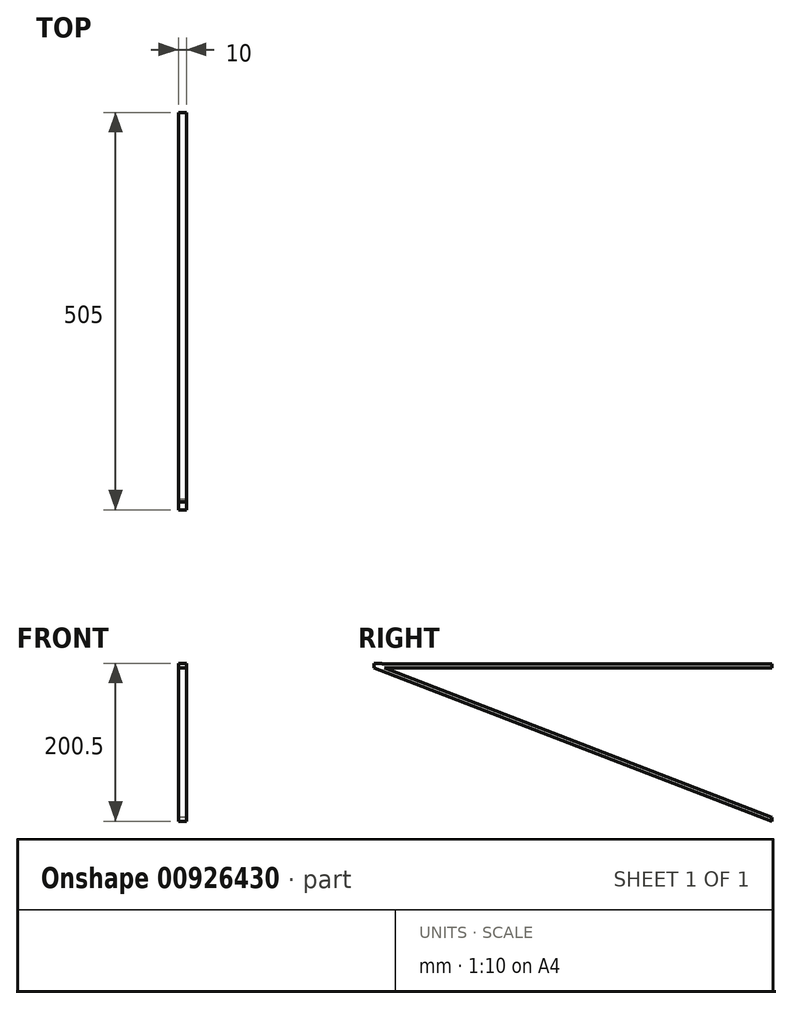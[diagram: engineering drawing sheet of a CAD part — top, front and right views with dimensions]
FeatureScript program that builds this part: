
annotation { "Feature Type Name" : "Feature", "Feature Type Description" : "" }
export const myFeature = defineFeature(function(context is Context, id is Id, definition is map)
    precondition{}
    {
        {
            var Q0;
            Q0=qCreatedBy(makeId("Front.planeOp"),FACE);
            var sketch = newSketch(context, id + "F0", { "sketchPlane" : qUnion([Q0])});
            skLineSegment(sketch, "E0", {"start": v(0, 0) * mm, "end": v(-5, 0) * mm});
            skLineSegment(sketch, "E1.MirrorCS", {"start": v(0, 0) * mm, "end": v(5, 0) * mm});
            skLineSegment(sketch, "E2", {"start": v(5, 0) * mm, "end": v(5, -200) * mm});
            skLineSegment(sketch, "E3.MirrorCS", {"start": v(-5, 0) * mm, "end": v(-5, -200) * mm});
            skLineSegment(sketch, "E4", {"start": v(5, -200) * mm, "end": v(-5, -200) * mm});
            skPoint(sketch, "E5", {"position": v(5, 0) * mm});
            skPoint(sketch, "E6", {"position": v(-5, 0) * mm});
            skSolve(sketch);
        }
        {
            var Q0;
            Q0=makeQuery(id+"F0.imprint","IMPRINT",FACE,{"disambiguationData":[TD([[makeQuery(id+"F0.imprint","IMPRINT",EDGE,{"derivedFrom":sQuery(id+"F0.wireOp",EDGE,"E0")}),1.0]])]});
            extrude(context, id + "F1", {"entities" : qUnion([Q0]), "depth" : 505 * mm, "offsetDistance" : 25 * mm});
        }
        {
            var Q0;
            Q0=qSketchRegion(id+"F0",true);
            extrude(context, id + "F2", {"entities" : qUnion([Q0]), "operationType" : NewBodyOperationType.ADD, "depth" : 500.5 * mm, "offsetDistance" : 25 * mm});
        }
        {
            var Q0;
            Q0=makeQuery(id+"F1.opExtrude","SWEPT_FACE",FACE,{"disambiguationData":[OSD([sQuery(id+"F0.wireOp",EDGE,"E3.MirrorCS")])]});
            var sketch = newSketch(context, id + "F3", { "sketchPlane" : qUnion([Q0])});
            skLineSegment(sketch, "E7", {"start": v(505, 0) * mm, "end": v(505, -5) * mm});
            skLineSegment(sketch, "E8", {"start": v(0, 0) * mm, "end": v(0, -5) * mm});
            skLineSegment(sketch, "E9", {"start": v(0, -5) * mm, "end": v(505, -5) * mm});
            skLineSegment(sketch, "E10", {"start": v(0, -200) * mm, "end": v(0, -195) * mm});
            skLineSegment(sketch, "E11", {"start": v(0, -195) * mm, "end": v(505, 0) * mm});
            skLineSegment(sketch, "E12", {"start": v(0, -200) * mm, "end": v(505, -5) * mm});
            skPoint(sketch, "E13", {"position": v(492.05, -5) * mm});
            skLineSegment(sketch, "E14", {"start": v(492.05, -5) * mm, "end": v(331.35, -5) * mm});
            skLineSegment(sketch, "E15", {"start": v(331.35, -5) * mm, "end": v(333.85, -5) * mm});
            skLineSegment(sketch, "E16", {"start": v(331.35, -5) * mm, "end": v(328.85, -5) * mm});
            skLineSegment(sketch, "E17", {"start": v(328.85, -5) * mm, "end": v(328.85, -65.32) * mm});
            skLineSegment(sketch, "E18", {"start": v(333.85, -5) * mm, "end": v(333.85, -66.09) * mm});
            skLineSegment(sketch, "E19", {"start": v(331.35, -5) * mm, "end": v(170.65, -5) * mm});
            skLineSegment(sketch, "E20", {"start": v(170.65, -5) * mm, "end": v(173.15, -5) * mm});
            skLineSegment(sketch, "E21", {"start": v(170.65, -5) * mm, "end": v(168.15, -5) * mm});
            skLineSegment(sketch, "E22", {"start": v(168.15, -5) * mm, "end": v(168.15, -130.07) * mm});
            skLineSegment(sketch, "E23", {"start": v(173.15, -7.7) * mm, "end": v(173.15, -128.14) * mm});
            skLineSegment(sketch, "E24", {"start": v(331.35, -67.05) * mm, "end": v(331.35, -83.15) * mm});
            skLineSegment(sketch, "E25", {"start": v(179.81, -5) * mm, "end": v(328.85, -65.32) * mm});
            skLineSegment(sketch, "E26", {"start": v(172.21, -7.32) * mm, "end": v(325.44, -69.33) * mm});
            skSolve(sketch);
        }
        {
            var Q0;
            {var subQ0=sQuery(id+"F3.wireOp",EDGE,"E17");Q0=makeQuery(id+"F3.imprint","IMPRINT",FACE,{"disambiguationData":[TD([[makeQuery(id+"F3.imprint","IMPRINT",EDGE,{"derivedFrom":subQ0}),-1.0]])]});}
            var Q1;
            {var subQ0=sQuery(id+"F3.wireOp",EDGE,"E23");Q1=makeQuery(id+"F3.imprint","IMPRINT",FACE,{"disambiguationData":[TD([[makeQuery(id+"F3.imprint","IMPRINT",EDGE,{"derivedFrom":subQ0}),1.0]])]});}
            var Q2;
            {var subQ3=sQuery(id+"F3.wireOp",EDGE,"E22");Q2=makeQuery(id+"F3.imprint","IMPRINT",FACE,{"disambiguationData":[TD([[makeQuery(id+"F3.imprint","IMPRINT",EDGE,{"derivedFrom":subQ3}),-1.0]])]});}
            var Q3;
            {var subQ0=sQuery(id+"F3.wireOp",EDGE,"E18");Q3=makeQuery(id+"F3.imprint","IMPRINT",FACE,{"disambiguationData":[TD([[makeQuery(id+"F3.imprint","IMPRINT",EDGE,{"derivedFrom":subQ0}),1.0]])]});}
            extrude(context, id + "F4", {"entities" : qUnion([Q0, Q1, Q2, Q3]), "operationType" : NewBodyOperationType.REMOVE, "endBound" : BoundingType.UP_TO_NEXT, "oppositeDirection" : true, "depth" : 25 * mm, "offsetDistance" : 25 * mm});
        }
        {
            var Q0;
            {var subQ1=sQuery(id+"F0.wireOp",EDGE,"E3.MirrorCS");var subQ2=makeQuery(id+"F1.opExtrude","SWEPT_EDGE",EDGE,{"disambiguationData":[OSD([subQ1,sQuery(id+"F0.wireOp",EDGE,"E4")])]});Q0=makeQuery(id+"F3.imprint","IMPRINT",FACE,{"disambiguationData":[TD([[makeQuery(id+"F3.imprint","IMPRINT",EDGE,{"derivedFrom":subQ2}),-1.0]])]});}
            extrude(context, id + "F5", {"entities" : qUnion([Q0]), "operationType" : NewBodyOperationType.REMOVE, "endBound" : BoundingType.UP_TO_NEXT, "oppositeDirection" : true, "depth" : 25 * mm, "offsetDistance" : 25 * mm});
        }
        {
            var Q0;
            Q0=makeQuery(id+"F1.opExtrude","SWEPT_FACE",FACE,{"disambiguationData":[OSD([sQuery(id+"F0.wireOp",EDGE,"E3.MirrorCS")])]});
            var sketch = newSketch(context, id + "F6", { "sketchPlane" : qUnion([Q0])});
            skLineSegment(sketch, "E27", {"start": v(168.15, -5) * mm, "end": v(179.81, -5) * mm});
            skLineSegment(sketch, "E28", {"start": v(328.85, -5) * mm, "end": v(333.85, -5) * mm});
            skLineSegment(sketch, "E29", {"start": v(325.44, -69.33) * mm, "end": v(333.85, -66.09) * mm});
            skLineSegment(sketch, "E30", {"start": v(168.15, -130.07) * mm, "end": v(173.15, -128.14) * mm});
            skSolve(sketch);
        }
        {
            var Q0;
            Q0=makeQuery(id+"F6.imprint","IMPRINT",FACE,{"disambiguationData":[TD([[makeQuery(id+"F6.imprint","IMPRINT",EDGE,{"derivedFrom":sQuery(id+"F6.wireOp",EDGE,"E27")}),-1.0]])]});
            extrude(context, id + "F7", {"entities" : qUnion([Q0]), "operationType" : NewBodyOperationType.REMOVE, "oppositeDirection" : true, "depth" : 3.5 * mm, "offsetDistance" : 25 * mm});
        }
        {
            var Q0;
            Q0=makeQuery(id+"F1.opExtrude","SWEPT_FACE",FACE,{"disambiguationData":[OSD([sQuery(id+"F0.wireOp",EDGE,"E0"),sQuery(id+"F0.wireOp",EDGE,"E1.MirrorCS")])]});
            var sketch = newSketch(context, id + "F8", { "sketchPlane" : qUnion([Q0])});
            skLineSegment(sketch, "E31.bottom", {"start": v(-5, -505) * mm, "end": v(5, -505) * mm});
            skLineSegment(sketch, "E31.top", {"start": v(-5, -495) * mm, "end": v(5, -495) * mm});
            skLineSegment(sketch, "E31.left", {"start": v(-5, -505) * mm, "end": v(-5, -495) * mm});
            skLineSegment(sketch, "E31.right", {"start": v(5, -505) * mm, "end": v(5, -495) * mm});
            skSolve(sketch);
        }
        {
            var Q0;
            Q0=makeQuery(id+"F1.opExtrude","SWEPT_FACE",FACE,{"disambiguationData":[OSD([sQuery(id+"F0.wireOp",EDGE,"E2")])]});
            var sketch = newSketch(context, id + "F9", { "sketchPlane" : qUnion([Q0])});
            skLineSegment(sketch, "E32", {"start": v(-173.15, -128.14) * mm, "end": v(-168.15, -130.07) * mm});
            skLineSegment(sketch, "E33", {"start": v(-325.44, -69.33) * mm, "end": v(-333.85, -66.09) * mm});
            skLineSegment(sketch, "E34", {"start": v(-333.85, -5) * mm, "end": v(-328.85, -5) * mm});
            skLineSegment(sketch, "E35", {"start": v(-168.15, -5) * mm, "end": v(-179.81, -5) * mm});
            skSolve(sketch);
        }
        {
            var Q0;
            Q0=makeQuery(id+"F8.imprint","IMPRINT",FACE,{"disambiguationData":[TD([[makeQuery(id+"F8.imprint","IMPRINT",EDGE,{"derivedFrom":sQuery(id+"F8.wireOp",EDGE,"E31.bottom")}),1.0]])]});
            extrude(context, id + "F10", {"entities" : qUnion([Q0]), "operationType" : NewBodyOperationType.ADD, "depth" : 0.5 * mm, "offsetDistance" : 25 * mm});
        }
        {
            var Q0;
            Q0=makeQuery(id+"F9.imprint","IMPRINT",FACE,{"disambiguationData":[TD([[makeQuery(id+"F9.imprint","IMPRINT",EDGE,{"derivedFrom":sQuery(id+"F9.wireOp",EDGE,"E32")}),1.0]])]});
            extrude(context, id + "F11", {"entities" : qUnion([Q0]), "operationType" : NewBodyOperationType.REMOVE, "oppositeDirection" : true, "depth" : 3.5 * mm, "offsetDistance" : 25 * mm});
        }
        {
            var Q0;
            {var subQ0=sQuery(id+"F3.wireOp",EDGE,"E9");Q0=makeQuery(id+"F11.boolean.opBoolean","MERGE",FACE,{"derivedFrom":[makeQuery(id+"F7.boolean.opBoolean","MERGE",FACE,{"derivedFrom":[makeQuery(id+"F4.boolean.opBoolean","COPY",FACE,{"derivedFrom":makeQuery(id+"F4.opExtrude","SWEPT_FACE",FACE,{"disambiguationData":[OSD([subQ0]),TDD([makeQuery(id+"F3.imprint","IMPRINT",EDGE,{"disambiguationData":[TD([[makeQuery(id+"F3.imprint","INTERSECT",VERTEX,{"derivedFrom":[subQ0,sQuery(id+"F3.wireOp",EDGE,"E22")]}),1.0]])],"derivedFrom":subQ0})])]})}),makeQuery(id+"F4.boolean.opBoolean","COPY",FACE,{"derivedFrom":makeQuery(id+"F4.opExtrude","SWEPT_FACE",FACE,{"disambiguationData":[OSD([subQ0]),TDD([makeQuery(id+"F3.imprint","IMPRINT",EDGE,{"disambiguationData":[TD([[makeQuery(id+"F3.imprint","INTERSECT",VERTEX,{"derivedFrom":[subQ0,sQuery(id+"F3.wireOp",EDGE,"E18")]}),-1.0]])],"derivedFrom":subQ0})])]})}),makeQuery(id+"F4.boolean.opBoolean","COPY",FACE,{"derivedFrom":makeQuery(id+"F4.opExtrude","SWEPT_FACE",FACE,{"disambiguationData":[OSD([subQ0]),TDD([makeQuery(id+"F3.imprint","IMPRINT",EDGE,{"disambiguationData":[TD([[makeQuery(id+"F3.imprint","INTERSECT",VERTEX,{"derivedFrom":[subQ0,sQuery(id+"F3.wireOp",EDGE,"E17")]}),1.0]])],"derivedFrom":subQ0})])]})})],"fromTools":[makeQuery(id+"F7.opExtrude","SWEPT_FACE",FACE,{"disambiguationData":[OSD([sQuery(id+"F6.wireOp",EDGE,"E27")])]}),makeQuery(id+"F7.opExtrude","SWEPT_FACE",FACE,{"disambiguationData":[OSD([sQuery(id+"F6.wireOp",EDGE,"E28")])]})]})],"fromTools":[makeQuery(id+"F11.opExtrude","SWEPT_FACE",FACE,{"disambiguationData":[OSD([sQuery(id+"F9.wireOp",EDGE,"E34")])]}),makeQuery(id+"F11.opExtrude","SWEPT_FACE",FACE,{"disambiguationData":[OSD([sQuery(id+"F9.wireOp",EDGE,"E35")])]})]});}
            var sketch = newSketch(context, id + "F12", { "sketchPlane" : qUnion([Q0])});
            skLineSegment(sketch, "E36", {"start": v(1.5, 0) * mm, "end": v(1.5, 492.05) * mm});
            skLineSegment(sketch, "E37", {"start": v(-1.5, 0) * mm, "end": v(1.5, 0) * mm});
            skLineSegment(sketch, "E38", {"start": v(-1.5, 0) * mm, "end": v(-1.5, 492.05) * mm});
            skLineSegment(sketch, "E39", {"start": v(1.5, 492.05) * mm, "end": v(-1.5, 492.05) * mm});
            skSolve(sketch);
        }
        {
            var Q0;
            {var subQ3=sQuery(id+"F12.wireOp",EDGE,"E39");Q0=makeQuery(id+"F12.imprint","IMPRINT",FACE,{"disambiguationData":[TD([[makeQuery(id+"F12.imprint","IMPRINT",EDGE,{"derivedFrom":subQ3}),1.0]])]});}
            var Q1;
            {var subQ1=sQuery(id+"F3.wireOp",EDGE,"E9");var subQ2=makeQuery(id+"F4.boolean.opBoolean","COPY",EDGE,{"derivedFrom":makeQuery(id+"F4.opExtrude","SWEPT_EDGE",EDGE,{"disambiguationData":[OSD([subQ1,sQuery(id+"F3.wireOp",EDGE,"E17")])]})});Q1=makeQuery(id+"F12.imprint","IMPRINT",FACE,{"disambiguationData":[TD([[makeQuery(id+"F12.imprint","IMPRINT",EDGE,{"derivedFrom":subQ2}),1.0]])]});}
            var Q2;
            {var subQ3=sQuery(id+"F12.wireOp",EDGE,"E37");Q2=makeQuery(id+"F12.imprint","IMPRINT",FACE,{"disambiguationData":[TD([[makeQuery(id+"F12.imprint","IMPRINT",EDGE,{"derivedFrom":subQ3}),-1.0]])]});}
            extrude(context, id + "F13", {"entities" : qUnion([Q0, Q1, Q2]), "operationType" : NewBodyOperationType.ADD, "depth" : 3 * mm, "offsetDistance" : 25 * mm});
        }
        {
            var Q0;
            {var subQ0=sQuery(id+"F3.wireOp",EDGE,"E11");Q0=makeQuery(id+"F11.boolean.opBoolean","MERGE",FACE,{"derivedFrom":[makeQuery(id+"F7.boolean.opBoolean","MERGE",FACE,{"derivedFrom":[makeQuery(id+"F4.boolean.opBoolean","COPY",FACE,{"derivedFrom":makeQuery(id+"F4.opExtrude","SWEPT_FACE",FACE,{"disambiguationData":[OSD([subQ0]),TDD([makeQuery(id+"F3.imprint","IMPRINT",EDGE,{"disambiguationData":[TD([[makeQuery(id+"F3.imprint","INTERSECT",VERTEX,{"derivedFrom":[subQ0,sQuery(id+"F3.wireOp",EDGE,"E22")]}),1.0]])],"derivedFrom":subQ0})])]})}),makeQuery(id+"F4.boolean.opBoolean","COPY",FACE,{"derivedFrom":makeQuery(id+"F4.opExtrude","SWEPT_FACE",FACE,{"disambiguationData":[OSD([subQ0]),TDD([makeQuery(id+"F3.imprint","IMPRINT",EDGE,{"disambiguationData":[TD([[makeQuery(id+"F3.imprint","INTERSECT",VERTEX,{"derivedFrom":[subQ0,sQuery(id+"F3.wireOp",EDGE,"E18")]}),-1.0]])],"derivedFrom":subQ0})])]})}),makeQuery(id+"F4.boolean.opBoolean","COPY",FACE,{"derivedFrom":makeQuery(id+"F4.opExtrude","SWEPT_FACE",FACE,{"disambiguationData":[OSD([subQ0]),TDD([makeQuery(id+"F3.imprint","IMPRINT",EDGE,{"disambiguationData":[TD([[makeQuery(id+"F3.imprint","INTERSECT",VERTEX,{"derivedFrom":[subQ0,sQuery(id+"F3.wireOp",EDGE,"E23")]}),-1.0]])],"derivedFrom":subQ0})])]})})],"fromTools":[makeQuery(id+"F7.opExtrude","SWEPT_FACE",FACE,{"disambiguationData":[OSD([sQuery(id+"F6.wireOp",EDGE,"E29")])]}),makeQuery(id+"F7.opExtrude","SWEPT_FACE",FACE,{"disambiguationData":[OSD([sQuery(id+"F6.wireOp",EDGE,"E30")])]})]})],"fromTools":[makeQuery(id+"F11.opExtrude","SWEPT_FACE",FACE,{"disambiguationData":[OSD([sQuery(id+"F9.wireOp",EDGE,"E32")])]}),makeQuery(id+"F11.opExtrude","SWEPT_FACE",FACE,{"disambiguationData":[OSD([sQuery(id+"F9.wireOp",EDGE,"E33")])]})]});}
            var sketch = newSketch(context, id + "F14", { "sketchPlane" : qUnion([Q0])});
            skLineSegment(sketch, "E40", {"start": v(-1.5, 70.24) * mm, "end": v(-1.5, -457.22) * mm});
            skLineSegment(sketch, "E41", {"start": v(1.5, 70.24) * mm, "end": v(1.5, -457.22) * mm});
            skLineSegment(sketch, "E42", {"start": v(1.5, -457.22) * mm, "end": v(-1.5, -457.22) * mm});
            skLineSegment(sketch, "E43", {"start": v(1.5, 70.24) * mm, "end": v(-1.5, 70.24) * mm});
            skSolve(sketch);
        }
        {
            var Q0;
            {var subQ3=sQuery(id+"F14.wireOp",EDGE,"E43");Q0=makeQuery(id+"F14.imprint","IMPRINT",FACE,{"disambiguationData":[TD([[makeQuery(id+"F14.imprint","IMPRINT",EDGE,{"derivedFrom":subQ3}),1.0]])]});}
            var Q1;
            {var subQ1=sQuery(id+"F3.wireOp",EDGE,"E11");var subQ2=makeQuery(id+"F4.boolean.opBoolean","COPY",EDGE,{"derivedFrom":makeQuery(id+"F4.opExtrude","SWEPT_EDGE",EDGE,{"disambiguationData":[OSD([subQ1,sQuery(id+"F3.wireOp",EDGE,"E23")])]})});Q1=makeQuery(id+"F14.imprint","IMPRINT",FACE,{"disambiguationData":[TD([[makeQuery(id+"F14.imprint","IMPRINT",EDGE,{"derivedFrom":subQ2}),1.0]])]});}
            var Q2;
            {var subQ1=sQuery(id+"F3.wireOp",EDGE,"E18");var subQ2=sQuery(id+"F3.wireOp",EDGE,"E11");var subQ3=makeQuery(id+"F4.boolean.opBoolean","COPY",EDGE,{"derivedFrom":makeQuery(id+"F4.opExtrude","SWEPT_EDGE",EDGE,{"disambiguationData":[OSD([subQ2,subQ1])]})});Q2=makeQuery(id+"F14.imprint","IMPRINT",FACE,{"disambiguationData":[TD([[makeQuery(id+"F14.imprint","IMPRINT",EDGE,{"derivedFrom":subQ3}),1.0]])]});}
            extrude(context, id + "F15", {"entities" : qUnion([Q0, Q1, Q2]), "operationType" : NewBodyOperationType.ADD, "depth" : 3 * mm, "offsetDistance" : 25 * mm});
        }
        {
            var Q0;
            Q0=makeQuery(id+"F15.opExtrude","SWEPT_FACE",FACE,{"disambiguationData":[OSD([sQuery(id+"F3.wireOp",EDGE,"E11"),sQuery(id+"F3.wireOp",EDGE,"E22")])]});
            extrude(context, id + "F16", {"entities" : qUnion([Q0]), "operationType" : NewBodyOperationType.ADD, "depth" : 40 * mm, "offsetDistance" : 25 * mm});
        }
        {
            var Q0;
            {var subQ0=sQuery(id+"F0.wireOp",EDGE,"E2");var subQ1=sQuery(id+"F0.wireOp",EDGE,"E3.MirrorCS");var subQ2=sQuery(id+"F0.wireOp",EDGE,"E4");Q0=makeQuery(id+"F4.boolean.opBoolean","SPLIT",FACE,{"disambiguationData":[TD([makeQuery(id+"F1.opExtrude","SWEPT_FACE",FACE,{"disambiguationData":[OSD([subQ2])]})])],"derivedFrom":makeQuery(id+"F1.opExtrude","CAP_FACE",FACE,{"disambiguationData":[OSD([sQuery(id+"F0.wireOp",EDGE,"E0"),sQuery(id+"F0.wireOp",EDGE,"E1.MirrorCS"),subQ0,subQ1,subQ2])],"isStart":true})});}
            var sketch = newSketch(context, id + "F17", { "sketchPlane" : qUnion([Q0])});
            skLineSegment(sketch, "E44.bottom", {"start": v(2.5, -195) * mm, "end": v(-3.07, -195) * mm});
            skLineSegment(sketch, "E44.top", {"start": v(2.5, -191.31) * mm, "end": v(-3.07, -191.31) * mm});
            skLineSegment(sketch, "E44.left", {"start": v(2.5, -195) * mm, "end": v(2.5, -191.31) * mm});
            skLineSegment(sketch, "E44.right", {"start": v(-3.07, -195) * mm, "end": v(-3.07, -191.31) * mm});
            skSolve(sketch);
        }
        {
            var Q0;
            Q0=qSketchRegion(id+"F17",true);
            extrude(context, id + "F18", {"entities" : qUnion([Q0]), "operationType" : NewBodyOperationType.REMOVE, "depth" : 25 * mm, "offsetDistance" : 25 * mm});
        }
        {
            var Q0;
            {var subQ0=sQuery(id+"F14.wireOp",EDGE,"E40");var subQ1=sQuery(id+"F3.wireOp",EDGE,"E22");var subQ2=sQuery(id+"F3.wireOp",EDGE,"E11");var subQ3=sQuery(id+"F3.wireOp",EDGE,"E18");var subQ5=sQuery(id+"F12.wireOp",EDGE,"E38");var subQ6=sQuery(id+"F3.wireOp",EDGE,"E9");var subQ7=sQuery(id+"F6.wireOp",EDGE,"E30");var subQ8=sQuery(id+"F6.wireOp",EDGE,"E29");var subQ9=sQuery(id+"F3.wireOp",EDGE,"E23");var subQ10=sQuery(id+"F3.wireOp",EDGE,"E26");var subQ13=sQuery(id+"F3.wireOp",EDGE,"E17");var subQ14=sQuery(id+"F3.wireOp",EDGE,"E25");Q0=makeQuery(id+"F16.boolean.opBoolean","MERGE",FACE,{"derivedFrom":[makeQuery(id+"F15.opExtrude","SWEPT_FACE",FACE,{"disambiguationData":[OSD([subQ0]),TDD([makeQuery(id+"F14.imprint","IMPRINT",EDGE,{"disambiguationData":[TD([[makeQuery(id+"F14.imprint","INTERSECT",VERTEX,{"derivedFrom":[makeQuery(id+"F4.boolean.opBoolean","COPY",EDGE,{"derivedFrom":makeQuery(id+"F4.opExtrude","SWEPT_EDGE",EDGE,{"disambiguationData":[OSD([subQ2,subQ1])]})}),subQ0]}),1.0]])],"derivedFrom":subQ0})])]}),makeQuery(id+"F15.boolean.opBoolean","MERGE",FACE,{"derivedFrom":[makeQuery(id+"F13.boolean.opBoolean","MERGE",FACE,{"derivedFrom":[makeQuery(id+"F7.boolean.opBoolean","COPY",FACE,{"derivedFrom":makeQuery(id+"F7.opExtrude","CAP_FACE",FACE,{"disambiguationData":[OSD([subQ13,subQ3,subQ1,subQ9,subQ14,subQ10,sQuery(id+"F6.wireOp",EDGE,"E27"),sQuery(id+"F6.wireOp",EDGE,"E28"),subQ8,subQ7])],"isStart":false})}),makeQuery(id+"F13.opExtrude","SWEPT_FACE",FACE,{"disambiguationData":[OSD([subQ5]),TDD([makeQuery(id+"F12.imprint","IMPRINT",EDGE,{"disambiguationData":[TD([[makeQuery(id+"F12.imprint","INTERSECT",VERTEX,{"derivedFrom":[makeQuery(id+"F4.boolean.opBoolean","COPY",EDGE,{"derivedFrom":makeQuery(id+"F4.opExtrude","SWEPT_EDGE",EDGE,{"disambiguationData":[OSD([subQ6,subQ1])]})}),subQ5]}),1.0]])],"derivedFrom":subQ5})])]}),makeQuery(id+"F13.opExtrude","SWEPT_FACE",FACE,{"disambiguationData":[OSD([subQ5]),TDD([makeQuery(id+"F12.imprint","IMPRINT",EDGE,{"disambiguationData":[TD([[makeQuery(id+"F12.imprint","INTERSECT",VERTEX,{"derivedFrom":[makeQuery(id+"F4.boolean.opBoolean","COPY",EDGE,{"derivedFrom":makeQuery(id+"F4.opExtrude","SWEPT_EDGE",EDGE,{"disambiguationData":[OSD([subQ6,subQ13])]})}),subQ5]}),1.0]])],"derivedFrom":subQ5})])]}),makeQuery(id+"F13.opExtrude","SWEPT_FACE",FACE,{"disambiguationData":[OSD([subQ5]),TDD([makeQuery(id+"F12.imprint","IMPRINT",EDGE,{"disambiguationData":[TD([[makeQuery(id+"F12.imprint","INTERSECT",VERTEX,{"derivedFrom":[makeQuery(id+"F4.boolean.opBoolean","COPY",EDGE,{"derivedFrom":makeQuery(id+"F4.opExtrude","SWEPT_EDGE",EDGE,{"disambiguationData":[OSD([subQ6,subQ3])]})}),subQ5]}),-1.0]])],"derivedFrom":subQ5})])]})]}),makeQuery(id+"F15.opExtrude","SWEPT_FACE",FACE,{"disambiguationData":[OSD([subQ0]),TDD([makeQuery(id+"F14.imprint","IMPRINT",EDGE,{"disambiguationData":[TD([[makeQuery(id+"F14.imprint","INTERSECT",VERTEX,{"derivedFrom":[makeQuery(id+"F4.boolean.opBoolean","COPY",EDGE,{"derivedFrom":makeQuery(id+"F4.opExtrude","SWEPT_EDGE",EDGE,{"disambiguationData":[OSD([subQ2,subQ9])]})}),subQ0]}),-1.0]])],"derivedFrom":subQ0})])]}),makeQuery(id+"F15.opExtrude","SWEPT_FACE",FACE,{"disambiguationData":[OSD([subQ0]),TDD([makeQuery(id+"F14.imprint","IMPRINT",EDGE,{"disambiguationData":[TD([[makeQuery(id+"F14.imprint","INTERSECT",VERTEX,{"derivedFrom":[makeQuery(id+"F4.boolean.opBoolean","COPY",EDGE,{"derivedFrom":makeQuery(id+"F4.opExtrude","SWEPT_EDGE",EDGE,{"disambiguationData":[OSD([subQ2,subQ3])]})}),subQ0]}),-1.0]])],"derivedFrom":subQ0})])]})]}),makeQuery(id+"F16.opExtrude","SWEPT_FACE",FACE,{"disambiguationData":[OSD([subQ2,subQ1,subQ0])]})]});}
            extrude(context, id + "F19", {"entities" : qUnion([Q0]), "operationType" : NewBodyOperationType.REMOVE, "oppositeDirection" : true, "depth" : 25 * mm, "offsetDistance" : 25 * mm});
        }
    });
